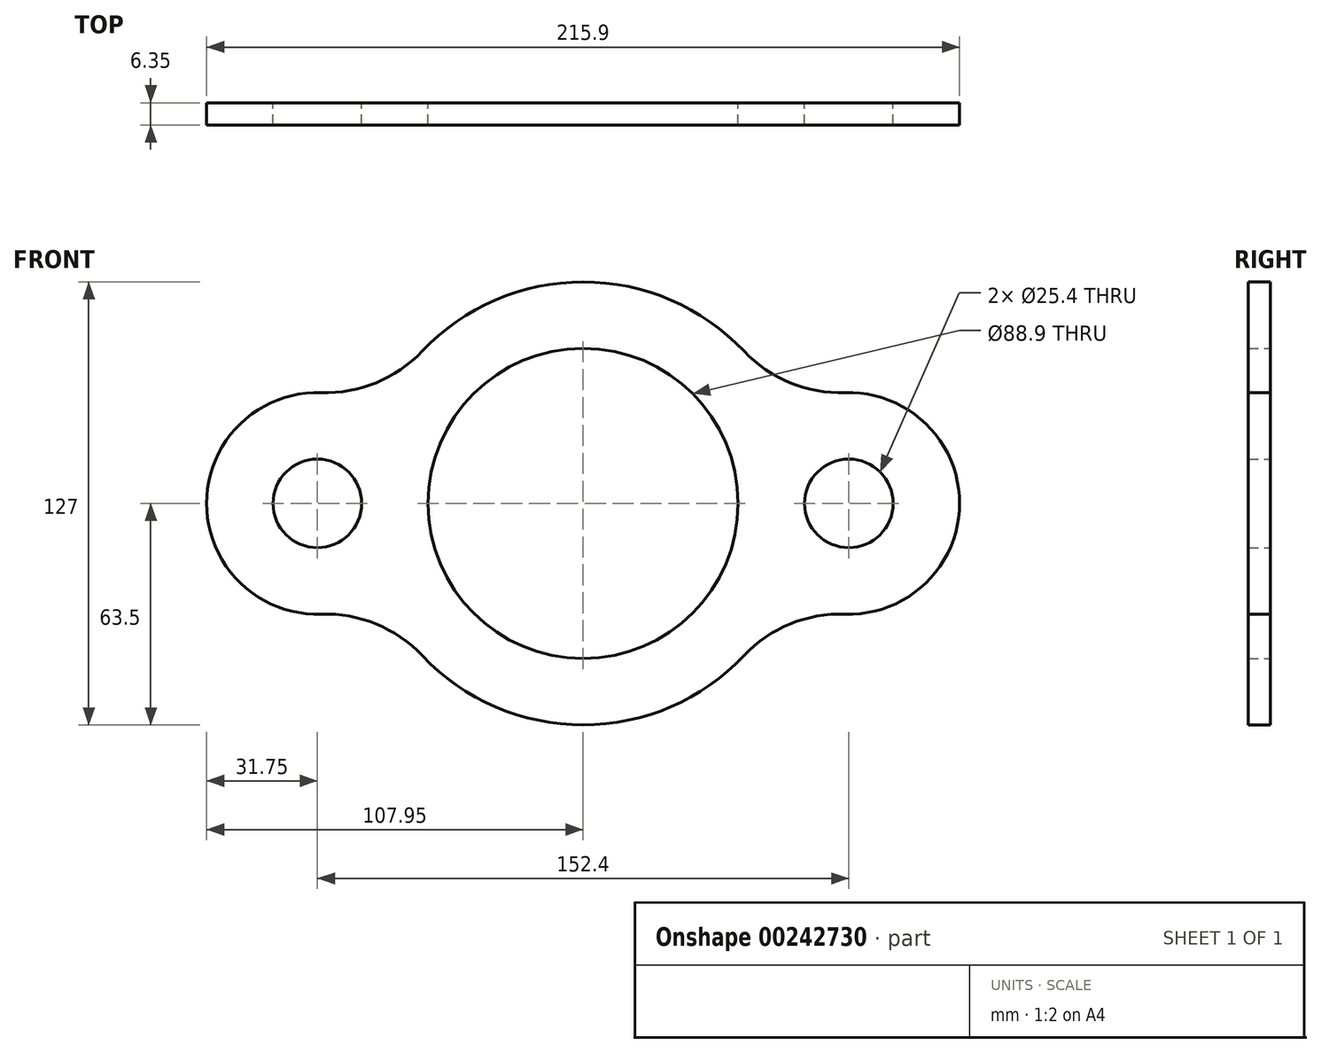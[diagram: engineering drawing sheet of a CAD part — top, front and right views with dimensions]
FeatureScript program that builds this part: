
annotation { "Feature Type Name" : "Feature", "Feature Type Description" : "" }
export const myFeature = defineFeature(function(context is Context, id is Id, definition is map)
    precondition{}
    {
        {
            var Q0;
            Q0=qCreatedBy(makeId("Front.planeOp"),FACE);
            var sketch = newSketch(context, id + "F0", { "sketchPlane" : qUnion([Q0])});
            skArc(sketch, "E0", {"start": v(-46.14, -43.63) * mm, "mid": v(0, -63.5) * mm, "end": v(46.14, -43.63) * mm});
            skCircle(sketch, "E1", {"center": v(0, 0) * mm, "radius": 44.45 * mm});
            skArc(sketch, "E2", {"start": v(-75.12, 31.73) * mm, "mid": v(-107.95, 0) * mm, "end": v(-75.12, -31.73) * mm});
            skCircle(sketch, "E3", {"center": v(-76.2, 0) * mm, "radius": 12.7 * mm});
            skArc(sketch, "E4", {"start": v(75.12, -31.73) * mm, "mid": v(107.95, 0) * mm, "end": v(75.12, 31.73) * mm});
            skCircle(sketch, "E5", {"center": v(76.2, 0) * mm, "radius": 12.7 * mm});
            skArc(sketch, "E6.trimOffspring", {"start": v(46.14, 43.63) * mm, "mid": v(0, 63.5) * mm, "end": v(-46.14, 43.63) * mm});
            skPoint(sketch, "E7.visualSharp", {"position": v(-57.94, 25.98) * mm});
            skArc(sketch, "E7.filletArc", {"start": v(-75.12, 31.73) * mm, "mid": v(-59.35, 34.56) * mm, "end": v(-46.14, 43.63) * mm});
            skPoint(sketch, "E8.visualSharp", {"position": v(57.94, 25.98) * mm});
            skArc(sketch, "E8.filletArc", {"start": v(46.14, 43.63) * mm, "mid": v(59.35, 34.56) * mm, "end": v(75.12, 31.73) * mm});
            skPoint(sketch, "E9.visualSharp", {"position": v(-57.94, -25.98) * mm});
            skArc(sketch, "E9.filletArc", {"start": v(-46.14, -43.63) * mm, "mid": v(-59.35, -34.56) * mm, "end": v(-75.12, -31.73) * mm});
            skPoint(sketch, "E10.visualSharp", {"position": v(57.94, -25.98) * mm});
            skArc(sketch, "E10.filletArc", {"start": v(75.12, -31.73) * mm, "mid": v(59.35, -34.56) * mm, "end": v(46.14, -43.63) * mm});
            skSolve(sketch);
        }
        {
            var Q0;
            Q0=makeQuery(id+"F0.imprint","IMPRINT",FACE,{"disambiguationData":[TD([[makeQuery(id+"F0.imprint","IMPRINT",EDGE,{"derivedFrom":sQuery(id+"F0.wireOp",EDGE,"E0")}),1.0]])]});
            extrude(context, id + "F1", {"entities" : qUnion([Q0]), "depth" : 6.35 * mm});
        }
    });
